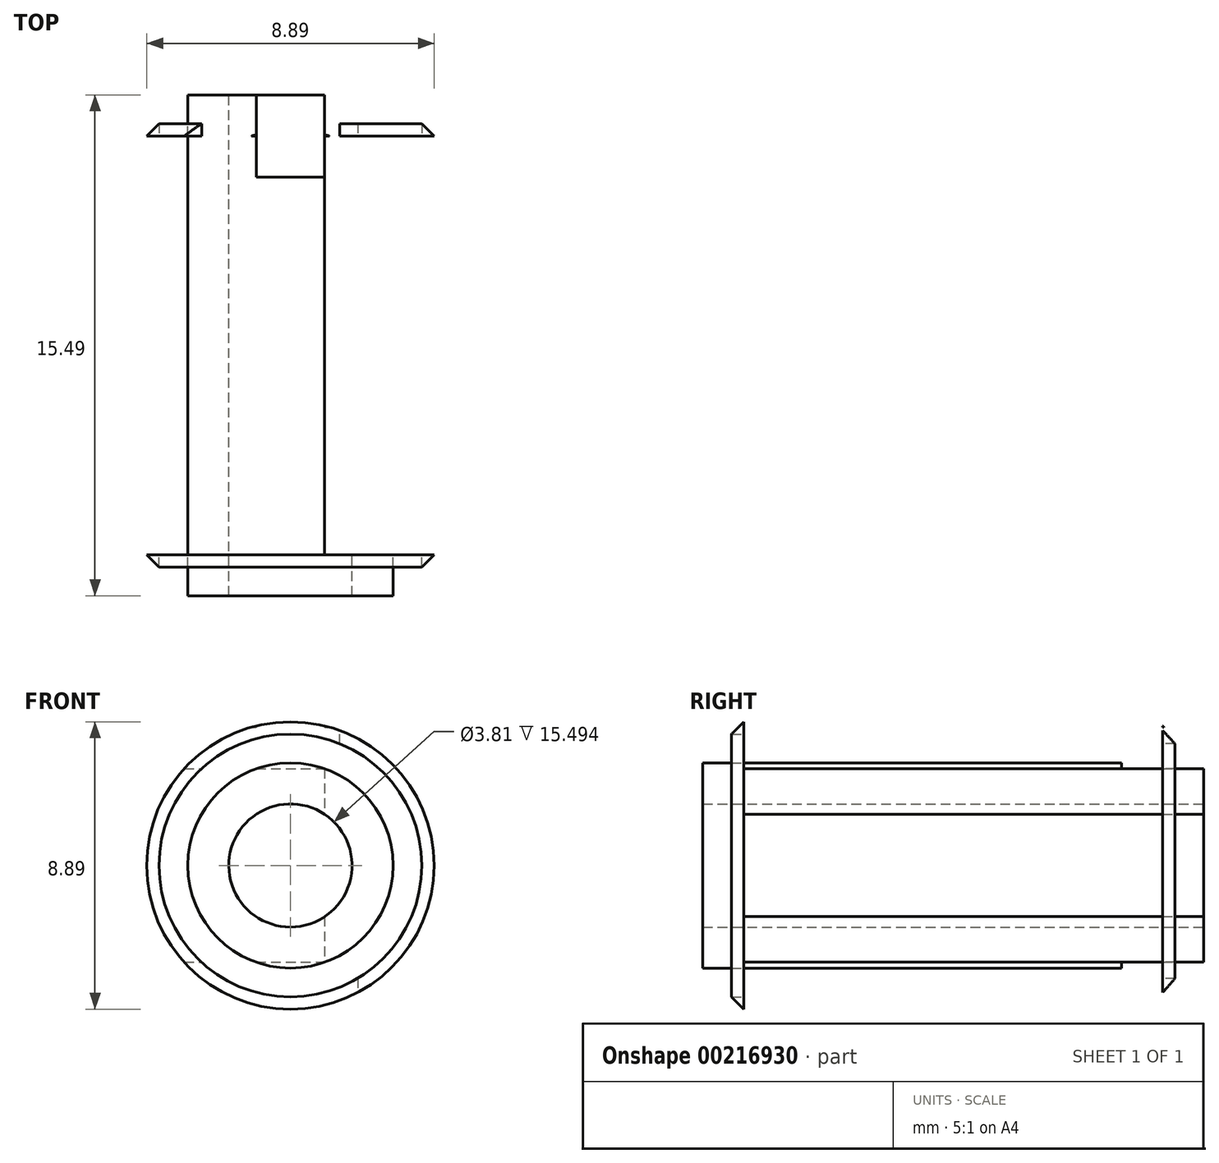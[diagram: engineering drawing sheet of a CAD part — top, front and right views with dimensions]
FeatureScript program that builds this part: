
annotation { "Feature Type Name" : "Feature", "Feature Type Description" : "" }
export const myFeature = defineFeature(function(context is Context, id is Id, definition is map)
    precondition{}
    {
        {
            var Q0;
            Q0=qCreatedBy(makeId("Front.planeOp"),FACE);
            var sketch = newSketch(context, id + "F0", { "sketchPlane" : qUnion([Q0])});
            skCircle(sketch, "E0", {"center": v(-18.79, 33.3) * mm, "radius": 3.18 * mm});
            skCircle(sketch, "E1", {"center": v(-18.79, 33.3) * mm, "radius": 1.9 * mm});
            skCircle(sketch, "E2", {"center": v(-18.79, 33.3) * mm, "radius": 41.28 * mm});
            skLineSegment(sketch, "E3", {"start": v(-18.79, 33.3) * mm, "end": v(-18.79, 74.58) * mm});
            skArc(sketch, "E4", {"start": v(-6.09, 96) * mm, "mid": v(-18.79, 108.7) * mm, "end": v(-31.49, 96) * mm});
            skFitSpline(sketch, "E5", {"points": [v(-31.49, 96) * mm, v(-18.79, 74.58) * mm], "startDerivative": vector(0, -40.17) * mm, "endDerivative": vector(0, -34.6) * mm});
            skArc(sketch, "E6.0.startCap", {"start": v(-2.91, 96) * mm, "mid": v(-6.09, 92.82) * mm, "end": v(-9.26, 96) * mm});
            skArc(sketch, "E6.0.left", {"start": v(-9.26, 96) * mm, "mid": v(-18.79, 105.52) * mm, "end": v(-28.31, 96) * mm});
            skArc(sketch, "E6.0.right", {"start": v(-2.91, 96) * mm, "mid": v(-18.79, 111.87) * mm, "end": v(-34.66, 96) * mm});
            skArc(sketch, "E6.1.endCap", {"start": v(-15.61, 74.58) * mm, "mid": v(-15.62, 74.52) * mm, "end": v(-15.62, 74.46) * mm});
            skFitSpline(sketch, "E6.1.left", {"points": [v(-28.31, 96) * mm, v(-28.31, 95.29) * mm, v(-28.23, 94.02) * mm, v(-27.91, 92.53) * mm, v(-27.47, 91.36) * mm, v(-26.9, 90.4) * mm, v(-26.23, 89.56) * mm, v(-25.4, 88.77) * mm, v(-24.43, 87.99) * mm, v(-23.33, 87.2) * mm, v(-22.11, 86.35) * mm, v(-20.83, 85.4) * mm, v(-19.53, 84.29) * mm, v(-18.26, 82.93) * mm, v(-17.14, 81.27) * mm, v(-16.27, 79.32) * mm, v(-15.73, 77.1) * mm, v(-15.61, 75.44) * mm, v(-15.61, 74.58) * mm]});
            skFitSpline(sketch, "E6.1.right", {"points": [v(-34.66, 96) * mm, v(-34.66, 95.04) * mm, v(-34.55, 93.22) * mm, v(-34.05, 90.78) * mm, v(-33.23, 88.63) * mm, v(-32.15, 86.78) * mm, v(-30.9, 85.23) * mm, v(-29.56, 83.95) * mm, v(-28.23, 82.9) * mm, v(-26.95, 81.98) * mm, v(-25.78, 81.17) * mm, v(-24.76, 80.4) * mm, v(-23.9, 79.67) * mm, v(-23.24, 78.94) * mm, v(-22.72, 78.18) * mm, v(-22.33, 77.3) * mm, v(-22.04, 76.16) * mm, v(-21.96, 75.15) * mm, v(-21.96, 74.58) * mm]});
            skArc(sketch, "E6.2.startCap", {"start": v(-15.61, 33.3) * mm, "mid": v(-18.79, 30.13) * mm, "end": v(-21.96, 33.3) * mm});
            skLineSegment(sketch, "E6.2.left", {"start": v(-21.96, 33.3) * mm, "end": v(-21.96, 74.58) * mm});
            skLineSegment(sketch, "E6.2.right", {"start": v(-15.61, 33.3) * mm, "end": v(-15.61, 74.58) * mm});
            skArc(sketch, "E7.trimOffspring", {"start": v(-21.96, 74.46) * mm, "mid": v(-21.96, 74.52) * mm, "end": v(-21.96, 74.58) * mm});
            skSolve(sketch);
        }
        {
            var Q0;
            Q0=makeQuery(id+"F0.imprint","IMPRINT",FACE,{"disambiguationData":[TD([[makeQuery(id+"F0.imprint","IMPRINT",EDGE,{"derivedFrom":sQuery(id+"F0.wireOp",EDGE,"E0")}),1.0]])]});
            extrude(context, id + "F1", {"entities" : qUnion([Q0]), "depth" : 12.95 * mm});
        }
        {
            var Q0;
            Q0=makeQuery(id+"F1.opExtrude","CAP_FACE",FACE,{"disambiguationData":[OSD([sQuery(id+"F0.wireOp",EDGE,"E0"),sQuery(id+"F0.wireOp",EDGE,"E1")])],"isStart":false});
            var sketch = newSketch(context, id + "F2", { "sketchPlane" : qUnion([Q0])});
            skCircle(sketch, "E8.0", {"center": v(-18.79, 33.3) * mm, "radius": 4.45 * mm});
            skSolve(sketch);
        }
        {
            var Q0;
            Q0=makeQuery(id+"F2.imprint","IMPRINT",FACE,{"disambiguationData":[TD([[makeQuery(id+"F2.imprint","IMPRINT",EDGE,{"derivedFrom":sQuery(id+"F2.wireOp",EDGE,"E8.0")}),1.0]])]});
            var Q1;
            Q1=makeQuery(id+"F2.imprint","IMPRINT",FACE,{"disambiguationData":[TD([[makeQuery(id+"F2.imprint","IMPRINT",EDGE,{"derivedFrom":makeQuery(id+"F1.opExtrude","CAP_EDGE",EDGE,{"disambiguationData":[OSD([sQuery(id+"F0.wireOp",EDGE,"E0")])],"isStart":false})}),1.0]])]});
            extrude(context, id + "F3", {"entities" : qUnion([Q0, Q1]), "operationType" : NewBodyOperationType.ADD, "depth" : 1.27 * mm});
        }
        {
            var Q0;
            Q0=makeQuery(id+"F3.opExtrude","CAP_EDGE",EDGE,{"disambiguationData":[OSD([sQuery(id+"F2.wireOp",EDGE,"E8.0")])],"isStart":false});
            chamfer(context, id + "F4", {"entities" : qUnion([Q0]), "width" : 1.27 * mm, "tangentPropagation" : true});
        }
        {
            var Q0;
            Q0=makeQuery(id+"F3.opExtrude","CAP_FACE",FACE,{"disambiguationData":[OSD([sQuery(id+"F0.wireOp",EDGE,"E1"),sQuery(id+"F2.wireOp",EDGE,"E8.0")])],"isStart":true});
            var sketch = newSketch(context, id + "F5", { "sketchPlane" : qUnion([Q0])});
            skCircle(sketch, "E9.0", {"center": v(18.79, 33.3) * mm, "radius": 4.06 * mm});
            skSolve(sketch);
        }
        {
            var Q0;
            Q0=makeQuery(id+"F5.imprint","IMPRINT",FACE,{"disambiguationData":[TD([[makeQuery(id+"F5.imprint","IMPRINT",EDGE,{"derivedFrom":sQuery(id+"F5.wireOp",EDGE,"E9.0")}),1.0]])]});
            extrude(context, id + "F6", {"entities" : qUnion([Q0]), "operationType" : NewBodyOperationType.REMOVE, "oppositeDirection" : true, "depth" : 25.4 * mm});
        }
        {
            var Q0;
            Q0=makeQuery(id+"F1.opExtrude","CAP_FACE",FACE,{"disambiguationData":[OSD([sQuery(id+"F0.wireOp",EDGE,"E0"),sQuery(id+"F0.wireOp",EDGE,"E1")])],"isStart":true});
            var sketch = newSketch(context, id + "F7", { "sketchPlane" : qUnion([Q0])});
            skCircle(sketch, "E10.0", {"center": v(18.79, 33.3) * mm, "radius": 4.45 * mm});
            skSolve(sketch);
        }
        {
            var Q0;
            Q0=makeQuery(id+"F7.imprint","IMPRINT",FACE,{"disambiguationData":[TD([[makeQuery(id+"F7.imprint","IMPRINT",EDGE,{"derivedFrom":sQuery(id+"F7.wireOp",EDGE,"E10.0")}),1.0]])]});
            var Q1;
            Q1=makeQuery(id+"F7.imprint","IMPRINT",FACE,{"disambiguationData":[TD([[makeQuery(id+"F7.imprint","IMPRINT",EDGE,{"derivedFrom":makeQuery(id+"F1.opExtrude","CAP_EDGE",EDGE,{"disambiguationData":[OSD([sQuery(id+"F0.wireOp",EDGE,"E0")])],"isStart":true})}),-1.0]])]});
            extrude(context, id + "F8", {"entities" : qUnion([Q0, Q1]), "operationType" : NewBodyOperationType.ADD, "depth" : 1.27 * mm});
        }
        {
            var Q0;
            Q0=makeQuery(id+"F8.opExtrude","CAP_EDGE",EDGE,{"disambiguationData":[OSD([sQuery(id+"F7.wireOp",EDGE,"E10.0")])],"isStart":false});
            chamfer(context, id + "F9", {"entities" : qUnion([Q0]), "width" : 1.27 * mm, "tangentPropagation" : true});
        }
        {
            var Q0;
            Q0=makeQuery(id+"F8.opExtrude","CAP_FACE",FACE,{"disambiguationData":[OSD([sQuery(id+"F0.wireOp",EDGE,"E1"),sQuery(id+"F7.wireOp",EDGE,"E10.0")])],"isStart":true});
            var sketch = newSketch(context, id + "F10", { "sketchPlane" : qUnion([Q0])});
            skCircle(sketch, "E11.0", {"center": v(-18.79, 33.3) * mm, "radius": 4.06 * mm});
            skSolve(sketch);
        }
        {
            var Q0;
            Q0=makeQuery(id+"F10.imprint","IMPRINT",FACE,{"disambiguationData":[TD([[makeQuery(id+"F10.imprint","IMPRINT",EDGE,{"derivedFrom":sQuery(id+"F10.wireOp",EDGE,"E11.0")}),1.0]])]});
            extrude(context, id + "F11", {"entities" : qUnion([Q0]), "operationType" : NewBodyOperationType.REMOVE, "oppositeDirection" : true, "depth" : 25.4 * mm});
        }
        {
            var Q0;
            Q0=makeQuery(id+"F8.opExtrude","CAP_FACE",FACE,{"disambiguationData":[OSD([sQuery(id+"F0.wireOp",EDGE,"E1"),sQuery(id+"F7.wireOp",EDGE,"E10.0")])],"isStart":false});
            var sketch = newSketch(context, id + "F12", { "sketchPlane" : qUnion([Q0])});
            skCircle(sketch, "E12", {"center": v(18.79, 33.3) * mm, "radius": 3.17 * mm});
            skPoint(sketch, "E12.first.point", {"position": v(18.76, 36.48) * mm});
            skPoint(sketch, "E12.second.point", {"position": v(21.57, 31.77) * mm});
            skPoint(sketch, "E12.third.point", {"position": v(15.9, 32) * mm});
            skLineSegment(sketch, "E13.left", {"start": v(17.73, 36.3) * mm, "end": v(17.73, 30.3) * mm});
            skLineSegment(sketch, "E13.right", {"start": v(19.85, 36.3) * mm, "end": v(19.85, 30.3) * mm});
            skLineSegment(sketch, "E14.bottom", {"start": v(17.73, 38.37) * mm, "end": v(19.85, 38.37) * mm});
            skLineSegment(sketch, "E14.top", {"start": v(17.73, 28.24) * mm, "end": v(19.85, 28.24) * mm});
            skLineSegment(sketch, "E14.left", {"start": v(17.73, 38.37) * mm, "end": v(17.73, 28.24) * mm});
            skLineSegment(sketch, "E14.right", {"start": v(19.85, 38.37) * mm, "end": v(19.85, 28.24) * mm});
            skSolve(sketch);
        }
        {
            var Q0;
            {var subQ5=sQuery(id+"F12.wireOp",EDGE,"E14.bottom");Q0=makeQuery(id+"F12.imprint","IMPRINT",FACE,{"disambiguationData":[TD([[makeQuery(id+"F12.imprint","IMPRINT",EDGE,{"derivedFrom":subQ5}),-1.0]])]});}
            var Q1;
            {var subQ0=sQuery(id+"F12.wireOp",EDGE,"E14.left");var subQ1=sQuery(id+"F12.wireOp",EDGE,"E12");var subQ2=makeQuery(id+"F12.imprint","INTERSECT",VERTEX,{"disambiguationData":[OD(1.0)],"derivedFrom":[subQ1,subQ0]});Q1=makeQuery(id+"F12.imprint","IMPRINT",FACE,{"disambiguationData":[TD([[makeQuery(id+"F12.imprint","IMPRINT",EDGE,{"disambiguationData":[TD([[subQ2,1.0]])],"derivedFrom":subQ1}),1.0]])]});}
            var Q2;
            {var subQ0=sQuery(id+"F12.wireOp",EDGE,"E14.left");var subQ1=makeQuery(id+"F8.opExtrude","CAP_EDGE",EDGE,{"disambiguationData":[OSD([sQuery(id+"F0.wireOp",EDGE,"E1")])],"isStart":false});var subQ2=makeQuery(id+"F12.imprint","INTERSECT",VERTEX,{"disambiguationData":[OD(0.0)],"derivedFrom":[subQ1,subQ0]});Q2=makeQuery(id+"F12.imprint","IMPRINT",FACE,{"disambiguationData":[TD([[makeQuery(id+"F12.imprint","IMPRINT",EDGE,{"disambiguationData":[TD([[subQ2,-1.0]])],"derivedFrom":subQ0}),1.0]])]});}
            var Q3;
            {var subQ0=sQuery(id+"F12.wireOp",EDGE,"E14.left");var subQ1=sQuery(id+"F12.wireOp",EDGE,"E12");var subQ2=makeQuery(id+"F12.imprint","INTERSECT",VERTEX,{"disambiguationData":[OD(0.0)],"derivedFrom":[subQ1,subQ0]});Q3=makeQuery(id+"F12.imprint","IMPRINT",FACE,{"disambiguationData":[TD([[makeQuery(id+"F12.imprint","IMPRINT",EDGE,{"disambiguationData":[TD([[subQ2,-1.0]])],"derivedFrom":subQ1}),1.0]])]});}
            var Q4;
            {var subQ5=sQuery(id+"F12.wireOp",EDGE,"E14.top");Q4=makeQuery(id+"F12.imprint","IMPRINT",FACE,{"disambiguationData":[TD([[makeQuery(id+"F12.imprint","IMPRINT",EDGE,{"derivedFrom":subQ5}),1.0]])]});}
            extrude(context, id + "F13", {"entities" : qUnion([Q0, Q1, Q2, Q3, Q4]), "operationType" : NewBodyOperationType.REMOVE, "oppositeDirection" : true, "depth" : 14.22 * mm});
        }
        {
            var Q0;
            {var subQ0=sQuery(id+"F7.wireOp",EDGE,"E10.0");var subQ1=sQuery(id+"F0.wireOp",EDGE,"E1");Q0=makeQuery(id+"F13.boolean.opBoolean","SPLIT",FACE,{"disambiguationData":[TD([makeQuery(id+"F13.opExtrude","SWEPT_FACE",FACE,{"disambiguationData":[OSD([sQuery(id+"F12.wireOp",EDGE,"E14.right")])]})])],"derivedFrom":makeQuery(id+"F8.opExtrude","CAP_FACE",FACE,{"disambiguationData":[OSD([subQ1,subQ0])],"isStart":false})});}
            var sketch = newSketch(context, id + "F14", { "sketchPlane" : qUnion([Q0])});
            skLineSegment(sketch, "E15.bottom", {"start": v(19.85, 36.3) * mm, "end": v(15.77, 36.3) * mm});
            skLineSegment(sketch, "E15.top", {"start": v(19.85, 37.58) * mm, "end": v(15.77, 37.58) * mm});
            skLineSegment(sketch, "E15.left", {"start": v(19.85, 36.3) * mm, "end": v(19.85, 37.58) * mm});
            skLineSegment(sketch, "E15.right", {"start": v(15.77, 36.3) * mm, "end": v(15.77, 37.58) * mm});
            skLineSegment(sketch, "E16.bottom", {"start": v(17.26, 36.3) * mm, "end": v(22.97, 36.3) * mm});
            skLineSegment(sketch, "E16.top", {"start": v(17.26, 37.58) * mm, "end": v(22.97, 37.58) * mm});
            skLineSegment(sketch, "E16.left", {"start": v(17.26, 36.3) * mm, "end": v(17.26, 37.58) * mm});
            skLineSegment(sketch, "E16.right", {"start": v(22.97, 36.3) * mm, "end": v(22.97, 37.58) * mm});
            skLineSegment(sketch, "E17.bottom", {"start": v(19.85, 30.3) * mm, "end": v(15.17, 30.3) * mm});
            skLineSegment(sketch, "E17.top", {"start": v(19.85, 28.58) * mm, "end": v(15.17, 28.58) * mm});
            skLineSegment(sketch, "E17.left", {"start": v(19.85, 30.3) * mm, "end": v(19.85, 28.58) * mm});
            skLineSegment(sketch, "E17.right", {"start": v(15.17, 30.3) * mm, "end": v(15.17, 28.58) * mm});
            skLineSegment(sketch, "E18.bottom", {"start": v(16.7, 30.3) * mm, "end": v(23.25, 30.3) * mm});
            skLineSegment(sketch, "E18.top", {"start": v(16.7, 28.58) * mm, "end": v(23.25, 28.58) * mm});
            skLineSegment(sketch, "E18.left", {"start": v(16.7, 30.3) * mm, "end": v(16.7, 28.58) * mm});
            skLineSegment(sketch, "E18.right", {"start": v(23.25, 30.3) * mm, "end": v(23.25, 28.58) * mm});
            skSolve(sketch);
        }
        {
            var Q0;
            {var subQ0=sQuery(id+"F14.wireOp",EDGE,"E15.left");Q0=makeQuery(id+"F14.imprint","IMPRINT",FACE,{"disambiguationData":[TD([[makeQuery(id+"F14.imprint","IMPRINT",EDGE,{"derivedFrom":subQ0}),1.0]])]});}
            var Q1;
            {var subQ0=sQuery(id+"F14.wireOp",EDGE,"E15.left");Q1=makeQuery(id+"F14.imprint","IMPRINT",FACE,{"disambiguationData":[TD([[makeQuery(id+"F14.imprint","IMPRINT",EDGE,{"derivedFrom":subQ0}),-1.0]])]});}
            var Q2;
            Q2=makeQuery(id+"F14.imprint","IMPRINT",FACE,{"disambiguationData":[TD([[makeQuery(id+"F14.imprint","IMPRINT",EDGE,{"derivedFrom":sQuery(id+"F14.wireOp",EDGE,"E15.bottom")}),-1.0]])]});
            var Q3;
            Q3=makeQuery(id+"F14.imprint","IMPRINT",FACE,{"disambiguationData":[TD([[makeQuery(id+"F14.imprint","IMPRINT",EDGE,{"derivedFrom":sQuery(id+"F14.wireOp",EDGE,"E17.bottom")}),1.0]])]});
            var Q4;
            {var subQ0=sQuery(id+"F14.wireOp",EDGE,"E17.left");Q4=makeQuery(id+"F14.imprint","IMPRINT",FACE,{"disambiguationData":[TD([[makeQuery(id+"F14.imprint","IMPRINT",EDGE,{"derivedFrom":subQ0}),-1.0]])]});}
            var Q5;
            {var subQ0=sQuery(id+"F14.wireOp",EDGE,"E17.left");Q5=makeQuery(id+"F14.imprint","IMPRINT",FACE,{"disambiguationData":[TD([[makeQuery(id+"F14.imprint","IMPRINT",EDGE,{"derivedFrom":subQ0}),1.0]])]});}
            extrude(context, id + "F15", {"entities" : qUnion([Q0, Q1, Q2, Q3, Q4, Q5]), "operationType" : NewBodyOperationType.REMOVE, "oppositeDirection" : true, "depth" : 2.54 * mm});
        }
    });
